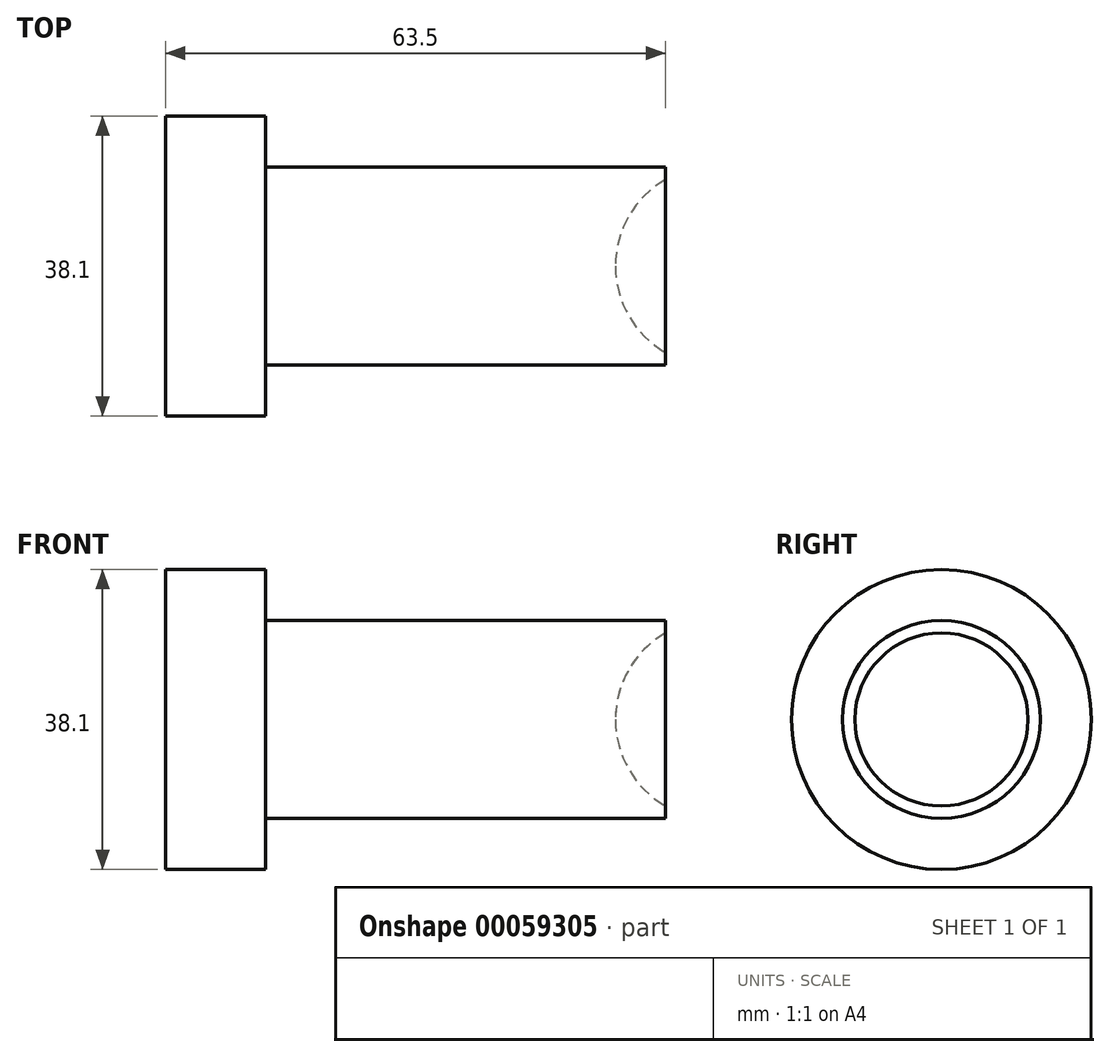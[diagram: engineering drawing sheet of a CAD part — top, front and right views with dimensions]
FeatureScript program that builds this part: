
annotation { "Feature Type Name" : "Feature", "Feature Type Description" : "" }
export const myFeature = defineFeature(function(context is Context, id is Id, definition is map)
    precondition{}
    {
        {
            var Q0;
            Q0=qCreatedBy(makeId("Front.planeOp"),FACE);
            var sketch = newSketch(context, id + "F0", { "sketchPlane" : qUnion([Q0])});
            skLineSegment(sketch, "E0.bottom", {"start": v(0, 0) * mm, "end": v(44.45, 0) * mm});
            skLineSegment(sketch, "E0.top", {"start": v(0, 12.57) * mm, "end": v(50.8, 12.57) * mm});
            skLineSegment(sketch, "E0.right", {"start": v(50.8, 11) * mm, "end": v(50.8, 12.57) * mm});
            skLineSegment(sketch, "E1.bottom", {"start": v(0, 0) * mm, "end": v(-12.7, 0) * mm});
            skLineSegment(sketch, "E1.top", {"start": v(0, 19.05) * mm, "end": v(-12.7, 19.05) * mm});
            skLineSegment(sketch, "E1.left", {"start": v(0, 12.57) * mm, "end": v(0, 19.05) * mm});
            skLineSegment(sketch, "E1.right", {"start": v(-12.7, 0) * mm, "end": v(-12.7, 19.05) * mm});
            skArc(sketch, "E2", {"start": v(50.8, 11) * mm, "mid": v(46.15, 6.35) * mm, "end": v(44.45, 0) * mm});
            skPoint(sketch, "E3.orphan", {"position": v(50.8, 0) * mm});
            skSolve(sketch);
        }
        {
            var Q0;
            Q0=makeQuery(id+"F0.imprint","IMPRINT",FACE,{"disambiguationData":[TD([[makeQuery(id+"F0.imprint","IMPRINT",EDGE,{"derivedFrom":sQuery(id+"F0.wireOp",EDGE,"E0.bottom")}),1.0]])]});
            var Q1;
            Q1=sQuery(id+"F0.wireOp",EDGE,"E0.bottom");
            revolve(context, id + "F1", {"entities" : qUnion([Q0]), "axis" : qUnion([Q1]), "revolveType" : RevolveType.FULL});
        }
    });
